FCSTD DOCUMENT  (FreeCAD 0.19R24365 (Git))
Label: Hub
License: All rights reserved
LicenseURL: http://en.wikipedia.org/wiki/All_rights_reserved
objects: App::Link×4, Spreadsheet::Sheet×1, App::Part×1
EXTERNAL_REF file=Hub_Flange.FCStd obj=Body
EXTERNAL_REF file=Hub_Flange_Cover_Front.FCStd obj=PadBody
EXTERNAL_REF file=../../Master_of_Puppets.FCStd obj=Hub
EXTERNAL_REF file=Hub_Flange_Cover_Back.FCStd obj=PadBody
EXTERNAL_REF file=Hub_StubAxleShaft.FCStd obj=Body

FEATURE [App::Link] Link  label="Flange"
  LinkedObject = -> <external Hub_Flange.FCStd>#Body
FEATURE [App::Link] Link001  label="Flange_Cover_Front"
  LinkPlacement = pos=(0,0,-75) rot=(0,0,1;0rad)
  LinkedObject = -> <external Hub_Flange_Cover_Front.FCStd>#PadBody
  Placement = pos=(0,0,-75) rot=(0,0,1;0rad)
  expr: .Placement.Base.z = Spreadsheet.RotorSideFlangeCoverZ
FEATURE [Spreadsheet::Sheet] Spreadsheet
  cells = A1=Inputs; A2=RotorSidePadWidth; B2(RotorSidePadWidth)==Master_of_Puppets#Hub.RotorSidePadWidth; A3=FrameSidePadWidth; B3(FrameSidePadWidth)==Master_of_Puppets#Hub.FrameSidePadWidth; A4=MiddlePadThickness; B4(MiddlePadThickness)==Master_of_Puppets#Hub.MiddlePadThickness; A5=CoverThickness; B5(CoverThickness)==Master_of_Puppets#Hub.CoverThickness; A6=StubAxleShaftLength; B6(StubAxleShaftLength)==Master_of_Puppets#Hub.StubAxleShaftLength; A7=Assembly; A8=RotorSideFlangeCoverZ; B8(RotorSideFlangeCoverZ)==-RotorSidePadWidth; A9=FrameSideFlangeCoverZ; B9(FrameSideFlangeCoverZ)==MiddlePadThickness + FrameSidePadWidth - CoverThickness; A10=StubAxleShaftZ; B10(StubAxleShaftZ)==StubAxleShaftLength
FEATURE [App::Link] Link002  label="Flange_Cover_Back"
  LinkPlacement = pos=(0,0,61) rot=(0,0,1;0rad)
  LinkedObject = -> <external Hub_Flange_Cover_Back.FCStd>#PadBody
  Placement = pos=(0,0,61) rot=(0,0,1;0rad)
  expr: .Placement.Base.z = Spreadsheet.FrameSideFlangeCoverZ
FEATURE [App::Link] Link003  label="StubAxleShaft"
  LinkPlacement = pos=(0,0,136) rot=(0,0,1;0rad)
  LinkedObject = -> <external Hub_StubAxleShaft.FCStd>#Body
  Placement = pos=(0,0,136) rot=(0,0,1;0rad)
  expr: .Placement.Base.z = Spreadsheet.StubAxleShaftZ
FEATURE [App::Part] Part  label="Hub"
  Group = -> [Link,Link001,Link002,Link003]
  Origin = -> Origin

RESOLVED EXTERNAL PARTS (link-assembly join: the EXTERNAL_REF files above that resolve inside this repo's crawl, each included once):
---- part ../../Master_of_Puppets.FCStd = doc fcstd_6404554055c4 (61625 chars; too large to inline — full recipe in that document) ----
---- part Hub_Flange.FCStd = doc fcstd_3618edf06f0d ----
FCSTD DOCUMENT  (FreeCAD 0.20R29177 (Git))
Label: Hub_Flange
License: All rights reserved
LicenseURL: http://en.wikipedia.org/wiki/All_rights_reserved
objects: Sketcher::SketchObject×5, PartDesign::Pad×3, PartDesign::Pocket×2, PartDesign::Plane×1, PartDesign::PolarPattern×1, PartDesign::Body×1, Spreadsheet::Sheet×1
note: 18 computed .brp shape members not serialized (recipe doc carries the construction recipe); baked Part::Feature solids carry a one-line shape summary decoded from their .brp
EXTERNAL_REF file=../../Master_of_Puppets.FCStd obj=Hub

FEATURE [Sketcher::SketchObject] Sketch  label="MiddlePadSketch"
  FullyConstrained = true
  MapMode = 5
  Support = -> [XY_Plane]
  expr: Constraints[1] = Spreadsheet.MiddlePadRadius
  sketch-geometry (1):
    g0: Circle CenterX=0 CenterY=0 CenterZ=0 NormalX=0 NormalY=0 NormalZ=1 AngleXU=0 Radius=71
  constraints (2):
    c: Coincident(g0,g-1)
    c: Radius(g0) = 71
FEATURE [PartDesign::Pad] Pad  label="MiddlePad"
  AllowMultiFace = false
  Direction = (0,0,1)
  Length = 16
  Length2 = 100
  Profile = -> Sketch
  Type = 0
FEATURE [PartDesign::Plane] DatumPlane
  Length = 170.4
  Placement = pos=(0,0,16) rot=(0,0,1;0rad)
  ResizeMode = 0
  Width = 170.4
  expr: .Placement.Base.z = Pad.Length
FEATURE [Sketcher::SketchObject] Sketch001  label="HubHoleSketch"
  FullyConstrained = true
  MapMode = 5
  Placement = pos=(0,0,16) rot=(0,0,1;0rad)
  Support = -> [DatumPlane]
  expr: Constraints[0] = Spreadsheet.HubPitchCircleRadius
  expr: Constraints[1] = Spreadsheet.HubHolesRadius
  sketch-geometry (1):
    g0: Circle CenterX=0 CenterY=50 CenterZ=0 NormalX=0 NormalY=0 NormalZ=1 AngleXU=0 Radius=6
  constraints (3):
    c: Distance(g-1,g0) = 50
    c: Radius(g0) = 6
    c: PointOnObject(g0,g-2)
FEATURE [PartDesign::Pocket] Pocket  label="HubHole"
  AllowMultiFace = false
  BaseFeature = -> Pad
  Direction = (0,0,-1)
  Length = 16
  Length2 = 100
  Profile = -> Sketch001
  Type = 0
  expr: Length = Spreadsheet.MiddlePadThickness
FEATURE [Sketcher::SketchObject] Sketch002  label="InnerHoleSketch"
  FullyConstrained = false
  MapMode = 5
  Placement = pos=(0,0,16) rot=(0,0,1;0rad)
  Support = -> [DatumPlane]
  expr: Constraints[0] = Spreadsheet.RotorSidePadRadius - Spreadsheet.ProtrudingPadThickness
  sketch-geometry (1):
    g0: Circle CenterX=0 CenterY=0 CenterZ=0 NormalX=0 NormalY=0 NormalZ=1 AngleXU=0 Radius=23
  constraints (1):
    c: Radius(g0) = 23
FEATURE [PartDesign::Pocket] Pocket001  label="InnerHole"
  AllowMultiFace = false
  BaseFeature = -> Pocket
  Direction = (0,0,-1)
  Length = 16
  Length2 = 100
  Profile = -> Sketch002
  Type = 0
  expr: Length = Pad.Length
FEATURE [PartDesign::PolarPattern] PolarPattern
  Angle = 360
  Axis = -> Z_Axis
  BaseFeature = -> Pocket001
  Occurrences = 4
  Originals = -> [Pocket]
  expr: Occurrences = Spreadsheet.NumberOfHoles
FEATURE [Sketcher::SketchObject] Sketch004  label="FrameSidePadSketch"
  FullyConstrained = true
  MapMode = 5
  Placement = pos=(0,0,16) rot=(0,0,1;0rad)
  Support = -> [DatumPlane]
  expr: Constraints[1] = Spreadsheet.FrameSidePadRadius - Spreadsheet.ProtrudingPadThickness
  expr: Constraints[3] = Spreadsheet.FrameSidePadRadius
  sketch-geometry (2):
    g0: Circle CenterX=0 CenterY=0 CenterZ=0 NormalX=0 NormalY=0 NormalZ=1 AngleXU=0 Radius=27.5
    g1: Circle CenterX=0 CenterY=0 CenterZ=0 NormalX=0 NormalY=0 NormalZ=1 AngleXU=0 Radius=32.5
  constraints (4):
    c: Coincident(g0,g-1)
    c: Radius(g0) = 27.5
    c: Coincident(g1,g0)
    c: Radius(g1) = 32.5
FEATURE [PartDesign::Pad] Pad001  label="FrameSidePad"
  AllowMultiFace = false
  BaseFeature = -> PolarPattern
  Direction = (0,0,1)
  Length = 35
  Length2 = 100
  Profile = -> Sketch004
  Type = 0
  expr: Length = Spreadsheet.FrameSidePadWidth - Spreadsheet.CoverThickness
FEATURE [Sketcher::SketchObject] Sketch005  label="RotorSidePadSketch"
  FullyConstrained = true
  MapMode = 5
  Placement = pos=(0,0,0) rot=(0,1,0;3.14159rad)
  Support = -> [XY_Plane]
  expr: Constraints[1] = Spreadsheet.RotorSidePadRadius - Spreadsheet.ProtrudingPadThickness
  expr: Constraints[3] = Spreadsheet.RotorSidePadRadius
  sketch-geometry (2):
    g0: Circle CenterX=0 CenterY=0 CenterZ=0 NormalX=0 NormalY=0 NormalZ=1 AngleXU=0 Radius=23
    g1: Circle CenterX=0 CenterY=0 CenterZ=0 NormalX=0 NormalY=0 NormalZ=1 AngleXU=0 Radius=28
  constraints (4):
    c: Coincident(g0,g-1)
    c: Radius(g0) = 23
    c: Coincident(g1,g0)
    c: Radius(g1) = 28
FEATURE [PartDesign::Pad] Pad002  label="RotorSidePad"
  AllowMultiFace = false
  BaseFeature = -> Pad001
  Direction = (0,0,-1)
  Length = 30
  Length2 = 100
  Profile = -> Sketch005
  Type = 0
  expr: Length = Spreadsheet.RotorSidePadWidth - Spreadsheet.CoverThickness
FEATURE [PartDesign::Body] Body  label="Hub_Flange"
  Group = -> [Sketch,Pad,DatumPlane,Sketch001,Pocket,Sketch002,Pocket001,PolarPattern,Sketch004,Pad001,Sketch005,Pad002]
  Origin = -> Origin
  Tip = -> Pad002
FEATURE [Spreadsheet::Sheet] Spreadsheet
  cells = A1=Inputs; A2=HubPitchCircleRadius; B2(HubPitchCircleRadius)==Master_of_Puppets#Hub.HubPitchCircleRadius; A3=HubHolesRadius; B3(HubHolesRadius)==Master_of_Puppets#Hub.HubHolesRadius; A4=MiddlePadRadius; B4(MiddlePadRadius)==Master_of_Puppets#Hub.MiddlePadRadius; A5=MiddlePadThickness; B5(MiddlePadThickness)==Master_of_Puppets#Hub.MiddlePadThickness; A6=ProtrudingPadThickness; B6(ProtrudingPadThickness)==Master_of_Puppets#Hub.ProtrudingPadThickness; A7=CoverThickness; B7(CoverThickness)==Master_of_Puppets#Hub.CoverThickness; A8=FrameSidePadRadius; B8(FrameSidePadRadius)==Master_of_Puppets#Hub.FrameSidePadRadius; A9=FrameSidePadWidth; B9(FrameSidePadWidth)==Master_of_Puppets#Hub.FrameSidePadWidth; A10=RotorSidePadRadius; B10(RotorSidePadRadius)==Master_of_Puppets#Hub.RotorSidePadRadius; A11=RotorSidePadWidth; B11(RotorSidePadWidth)==Master_of_Puppets#Hub.RotorSidePadWidth; A12=NumberOfHoles; B12(NumberOfHoles)==Master_of_Puppets#Hub.NumberOfHoles
---- part Hub_Flange_Cover_Back.FCStd = doc fcstd_5901b2285114 ----
FCSTD DOCUMENT  (FreeCAD 0.19R24291 (Git))
Label: Hub_Flange_Cover_Back
License: All rights reserved
LicenseURL: http://en.wikipedia.org/wiki/All_rights_reserved
objects: Sketcher::SketchObject×1, PartDesign::Pad×1, PartDesign::Body×1, Spreadsheet::Sheet×1
note: 4 computed .brp shape members not serialized (recipe doc carries the construction recipe); baked Part::Feature solids carry a one-line shape summary decoded from their .brp
EXTERNAL_REF file=../../Master_of_Puppets.FCStd obj=Hub

FEATURE [Sketcher::SketchObject] Sketch
  FullyConstrained = true
  MapMode = 5
  Support = -> [XY_Plane001]
  expr: Constraints[3] = Spreadsheet.StubAxleShaftRadius
  expr: Constraints[1] = Spreadsheet.FrameSidePadRadius
  sketch-geometry (2):
    g0: Circle CenterX=0 CenterY=0 CenterZ=0 NormalX=0 NormalY=0 NormalZ=1 AngleXU=0 Radius=32.5
    g1: Circle CenterX=0 CenterY=0 CenterZ=0 NormalX=0 NormalY=0 NormalZ=1 AngleXU=0 Radius=18
  constraints (4):
    c: Coincident(g0,g-1)
    c: Radius(g0) = 32.5
    c: Coincident(g1,g-1)
    c: Radius(g1) = 18
FEATURE [PartDesign::Pad] Pad
  AllowMultiFace = false
  Direction = (1,1,1)
  Length = 10
  Length2 = 100
  Profile = -> Sketch
  Type = 0
  expr: Length = Spreadsheet.CoverThickness
FEATURE [PartDesign::Body] PadBody  label="Hub_Flange_Cover_Back"
  Group = -> [Sketch,Pad]
  Origin = -> Origin001
  Tip = -> Pad
FEATURE [Spreadsheet::Sheet] Spreadsheet
  cells = A1=Inputs; A2=CoverThickness; B2(CoverThickness)==Master_of_Puppets#Hub.CoverThickness; A3=FrameSidePadRadius; B3(FrameSidePadRadius)==Master_of_Puppets#Hub.FrameSidePadRadius; A4=StubAxleShaftRadius; B4(StubAxleShaftRadius)==Master_of_Puppets#Hub.StubAxleShaftRadius
---- part Hub_Flange_Cover_Front.FCStd = doc fcstd_f9d8e5a768ec ----
FCSTD DOCUMENT  (FreeCAD 0.19R24291 (Git))
Label: Hub_Flange_Cover_Front
License: All rights reserved
LicenseURL: http://en.wikipedia.org/wiki/All_rights_reserved
objects: Sketcher::SketchObject×1, PartDesign::Pad×1, PartDesign::Body×1, Spreadsheet::Sheet×1
note: 4 computed .brp shape members not serialized (recipe doc carries the construction recipe); baked Part::Feature solids carry a one-line shape summary decoded from their .brp
EXTERNAL_REF file=../../Master_of_Puppets.FCStd obj=Hub

FEATURE [Sketcher::SketchObject] Sketch
  FullyConstrained = true
  MapMode = 5
  Support = -> [XY_Plane001]
  expr: Constraints[1] = Spreadsheet.RotorSidePadRadius
  sketch-geometry (1):
    g0: Circle CenterX=0 CenterY=0 CenterZ=0 NormalX=0 NormalY=0 NormalZ=1 AngleXU=0 Radius=28
  constraints (2):
    c: Coincident(g0,g-1)
    c: Radius(g0) = 28
FEATURE [PartDesign::Pad] Pad
  AllowMultiFace = false
  Direction = (1,1,1)
  Length = 10
  Length2 = 100
  Profile = -> Sketch
  Type = 0
  expr: Length = Spreadsheet.CoverThickness
FEATURE [PartDesign::Body] PadBody  label="Hub_Flange_Cover_Front"
  Group = -> [Sketch,Pad]
  Origin = -> Origin001
  Placement = pos=(0,0,-40) rot=(0,0,1;0rad)
  Tip = -> Pad
  expr: .Placement.Base.z = -40
FEATURE [Spreadsheet::Sheet] Spreadsheet
  cells = A1=Inputs; A2=CoverThickness; B2(CoverThickness)==Master_of_Puppets#Hub.CoverThickness; A3=RotorSidePadRadius; B3(RotorSidePadRadius)==Master_of_Puppets#Hub.RotorSidePadRadius
---- part Hub_StubAxleShaft.FCStd = doc fcstd_8398643136de ----
FCSTD DOCUMENT  (FreeCAD 0.19R24365 (Git))
Label: Hub_StubAxleShaft
License: All rights reserved
LicenseURL: http://en.wikipedia.org/wiki/All_rights_reserved
objects: PartDesign::Plane×2, Sketcher::SketchObject×2, PartDesign::Pad×2, PartDesign::Body×1, Spreadsheet::Sheet×1
note: 9 computed .brp shape members not serialized (recipe doc carries the construction recipe); baked Part::Feature solids carry a one-line shape summary decoded from their .brp
EXTERNAL_REF file=../../Master_of_Puppets.FCStd obj=Hub
EXTERNAL_REF file=../../Master_of_Puppets.FCStd obj=Spreadsheet

FEATURE [PartDesign::Plane] DatumPlane001
  Length = 60
  ResizeMode = 0
  Width = 60
FEATURE [Sketcher::SketchObject] Sketch003
  FullyConstrained = false
  MapMode = 5
  Placement = pos=(0,0,0) rot=(0,1,0;3.14159rad)
  Support = -> [DatumPlane001]
  expr: Constraints[0] = Spreadsheet.StubAxleShaftRadius
  sketch-geometry (1):
    g0: Circle CenterX=-0.005294 CenterY=0 CenterZ=0 NormalX=0 NormalY=0 NormalZ=1 AngleXU=0 Radius=30
  constraints (1):
    c: Radius(g0) = 30
FEATURE [PartDesign::Pad] Pad002  label="OuterShaft"
  AllowMultiFace = false
  Direction = (1,1,1)
  Length = 81.6
  Length2 = 100
  Profile = -> Sketch003
  Type = 0
  expr: Length = Spreadsheet.OuterShaftWidth
FEATURE [PartDesign::Plane] DatumPlane002
  Length = 60
  Placement = pos=(0,0,-81.6) rot=(0,0,1;0rad)
  ResizeMode = 0
  Width = 60
  expr: .Placement.Base.z = -Pad002.Length
FEATURE [Sketcher::SketchObject] Sketch004
  FullyConstrained = false
  MapMode = 5
  Placement = pos=(0,0,-81.6) rot=(0,1,0;3.14159rad)
  Support = -> [DatumPlane002]
  expr: Constraints[0] = Spreadsheet.StubAxleShaftRadius - 10
  sketch-geometry (1):
    g0: Circle CenterX=-0.026582 CenterY=0 CenterZ=0 NormalX=0 NormalY=0 NormalZ=1 AngleXU=0 Radius=20
  constraints (1):
    c: Radius(g0) = 20
FEATURE [PartDesign::Pad] Pad003  label="InnerShaft"
  AllowMultiFace = false
  BaseFeature = -> Pad002
  Direction = (1,1,1)
  Length = 54.4
  Length2 = 100
  Profile = -> Sketch004
  Type = 0
  expr: Length = Spreadsheet.InnerShaftWidth
FEATURE [PartDesign::Body] Body  label="Hub_StubAxleShaft"
  Group = -> [DatumPlane001,Sketch003,Pad002,DatumPlane002,Sketch004,Pad003]
  Origin = -> Origin
  Tip = -> Pad003
FEATURE [Spreadsheet::Sheet] Spreadsheet
  cells = A1=Inputs; A2=RotorDiskRadius; B2(RotorDiskRadius)==Master_of_Puppets#Spreadsheet.RotorDiskRadius; A3=StubAxleShaftRadius; B3(StubAxleShaftRadius)==Master_of_Puppets#Hub.StubAxleShaftRadius; A4=FrameSidePadWidth; B4(FrameSidePadWidth)==Master_of_Puppets#Hub.FrameSidePadWidth; A5=MiddlePadThickness; B5(MiddlePadThickness)==Master_of_Puppets#Hub.MiddlePadThickness; A6=RotorSidePadWidth; B6(RotorSidePadWidth)==Master_of_Puppets#Hub.RotorSidePadWidth; A7=StubAxleShaftLength; B7(StubAxleShaftLength)==Master_of_Puppets#Hub.StubAxleShaftLength; A8=Calculated; A9=OuterShaftWidth; B9(OuterShaftWidth)==StubAxleShaftLength * 0.6; A10=InnerShaftWidth; B10(InnerShaftWidth)==StubAxleShaftLength * 0.4
